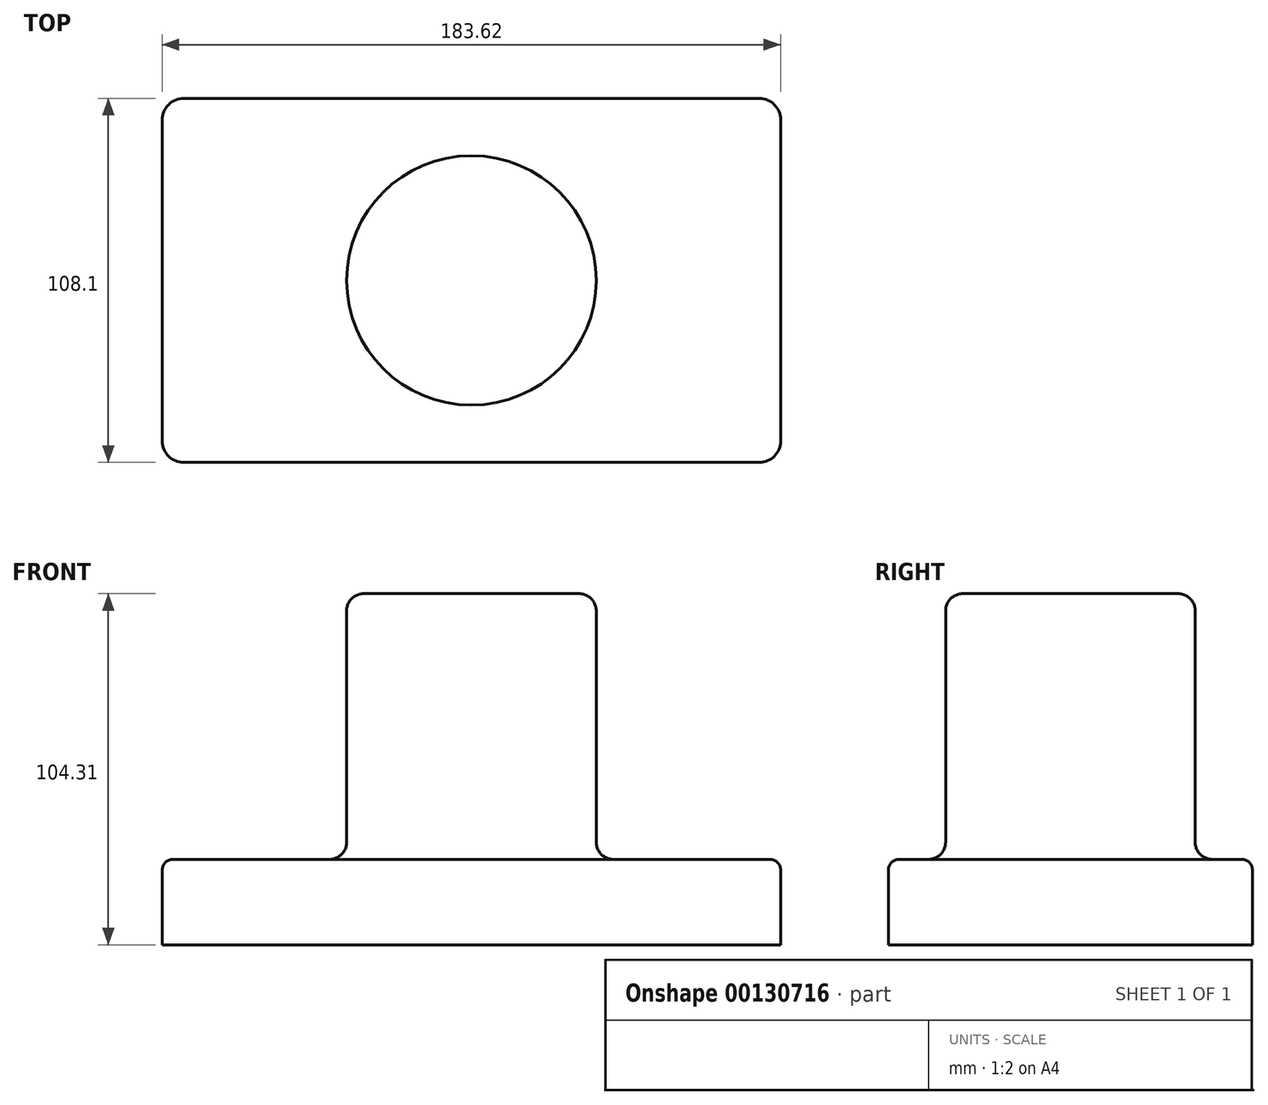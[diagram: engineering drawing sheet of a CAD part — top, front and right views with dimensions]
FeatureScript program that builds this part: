
annotation { "Feature Type Name" : "Feature", "Feature Type Description" : "" }
export const myFeature = defineFeature(function(context is Context, id is Id, definition is map)
    precondition{}
    {
        {
            var Q0;
            Q0=qCreatedBy(makeId("Top.planeOp"),FACE);
            var sketch = newSketch(context, id + "F0", { "sketchPlane" : qUnion([Q0])});
            skLineSegment(sketch, "E0.bottom", {"start": v(-91.8, 54.05) * mm, "end": v(91.8, 54.05) * mm});
            skLineSegment(sketch, "E0.top", {"start": v(-91.8, -54.05) * mm, "end": v(91.8, -54.05) * mm});
            skLineSegment(sketch, "E0.left", {"start": v(-91.8, 54.05) * mm, "end": v(-91.8, -54.05) * mm});
            skLineSegment(sketch, "E0.right", {"start": v(91.8, 54.05) * mm, "end": v(91.8, -54.05) * mm});
            skPoint(sketch, "E0.middle", {"position": v(0, 0) * mm});
            skSolve(sketch);
        }
        {
            var Q0;
            Q0=makeQuery(id+"F0.imprint","IMPRINT",FACE,{"disambiguationData":[TD([[makeQuery(id+"F0.imprint","IMPRINT",EDGE,{"derivedFrom":sQuery(id+"F0.wireOp",EDGE,"E0.bottom")}),-1.0]])]});
            extrude(context, id + "F1", {"entities" : qUnion([Q0]), "depth" : 25.4 * mm});
        }
        {
            var Q0;
            Q0=makeQuery(id+"F1.opExtrude","SWEPT_EDGE",EDGE,{"disambiguationData":[OSD([sQuery(id+"F0.wireOp",EDGE,"E0.top"),sQuery(id+"F0.wireOp",EDGE,"E0.left")])]});
            var Q1;
            Q1=makeQuery(id+"F1.opExtrude","SWEPT_EDGE",EDGE,{"disambiguationData":[OSD([sQuery(id+"F0.wireOp",EDGE,"E0.top"),sQuery(id+"F0.wireOp",EDGE,"E0.right")])]});
            var Q2;
            Q2=makeQuery(id+"F1.opExtrude","SWEPT_EDGE",EDGE,{"disambiguationData":[OSD([sQuery(id+"F0.wireOp",EDGE,"E0.bottom"),sQuery(id+"F0.wireOp",EDGE,"E0.right")])]});
            var Q3;
            Q3=makeQuery(id+"F1.opExtrude","SWEPT_EDGE",EDGE,{"disambiguationData":[OSD([sQuery(id+"F0.wireOp",EDGE,"E0.bottom"),sQuery(id+"F0.wireOp",EDGE,"E0.left")])]});
            fillet(context, id + "F2", {"entities" : qUnion([Q0, Q1, Q2, Q3]), "radius" : 6.35 * mm, "tangentPropagation" : true, "allowEdgeOverflow" : false});
        }
        {
            var Q0;
            Q0=makeQuery(id+"F1.opExtrude","CAP_FACE",FACE,{"disambiguationData":[OSD([sQuery(id+"F0.wireOp",EDGE,"E0.bottom"),sQuery(id+"F0.wireOp",EDGE,"E0.top"),sQuery(id+"F0.wireOp",EDGE,"E0.left"),sQuery(id+"F0.wireOp",EDGE,"E0.right")])],"isStart":false});
            var sketch = newSketch(context, id + "F3", { "sketchPlane" : qUnion([Q0])});
            skCircle(sketch, "E1", {"center": v(0, 0) * mm, "radius": 37.06 * mm});
            skSolve(sketch);
        }
        {
            var Q0;
            Q0 = qSketchRegion(id + "F3", true);
            extrude(context, id + "F4", {"entities" : qUnion([Q0]), "operationType" : NewBodyOperationType.ADD, "depth" : 78.9 * mm});
        }
        {
            var Q0;
            Q0=makeQuery(id+"F4.opExtrude","SWEPT_FACE",FACE,{"disambiguationData":[OSD([sQuery(id+"F3.wireOp",EDGE,"E1")])]});
            fillet(context, id + "F5", {"entities" : qUnion([Q0]), "radius" : 5.08 * mm, "tangentPropagation" : true, "allowEdgeOverflow" : false});
        }
        {
            var Q0;
            Q0=makeQuery(id+"F4.opExtrude","CAP_FACE",FACE,{"disambiguationData":[OSD([sQuery(id+"F3.wireOp",EDGE,"E1")])],"isStart":false});
            var Q1;
            Q1=makeQuery(id+"F1.opExtrude","CAP_EDGE",EDGE,{"disambiguationData":[OSD([sQuery(id+"F0.wireOp",EDGE,"E0.left")])],"isStart":false});
            fillet(context, id + "F6", {"entities" : qUnion([Q0, Q1]), "radius" : 3.17 * mm, "tangentPropagation" : true, "allowEdgeOverflow" : false});
        }
    });
